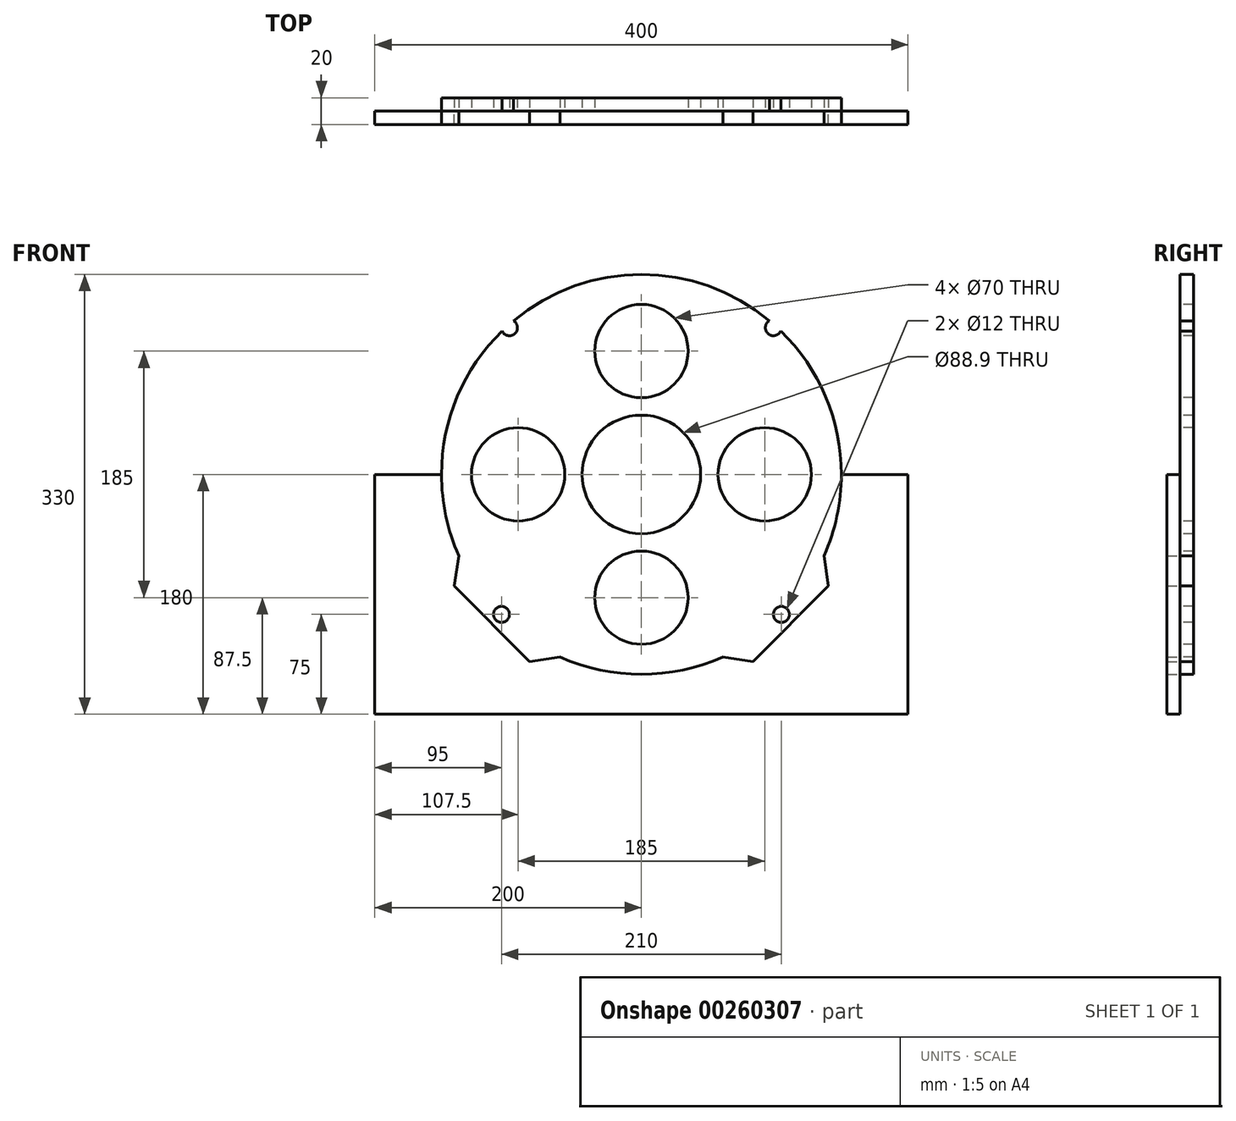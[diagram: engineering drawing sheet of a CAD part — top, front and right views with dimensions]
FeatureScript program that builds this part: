
annotation { "Feature Type Name" : "Feature", "Feature Type Description" : "" }
export const myFeature = defineFeature(function(context is Context, id is Id, definition is map)
    precondition{}
    {
        {
            var Q0;
            Q0=qCreatedBy(makeId("Front.planeOp"),FACE);
            var sketch = newSketch(context, id + "F0", { "sketchPlane" : qUnion([Q0])});
            skCircle(sketch, "E0", {"center": v(0, 0) * mm, "radius": 150 * mm});
            skCircle(sketch, "E1", {"center": v(0, 0) * mm, "radius": 140 * mm});
            skCircle(sketch, "E2", {"center": v(-99, 110) * mm, "radius": 6 * mm});
            skCircle(sketch, "E3.MirrorC", {"center": v(99, 110) * mm, "radius": 6 * mm});
            skCircle(sketch, "E4", {"center": v(105, -105) * mm, "radius": 6 * mm});
            skCircle(sketch, "E5.MirrorC", {"center": v(-105, -105) * mm, "radius": 6 * mm});
            skArc(sketch, "E6", {"start": v(-108.87, 103.18) * mm, "mid": v(-107.03, 118.92) * mm, "end": v(-91.18, 119.1) * mm});
            skArc(sketch, "E7", {"start": v(91.18, 119.1) * mm, "mid": v(107.03, 118.92) * mm, "end": v(108.87, 103.18) * mm});
            skLineSegment(sketch, "E8", {"start": v(-105, -105) * mm, "end": v(-112.07, -112.07) * mm});
            skLineSegment(sketch, "E9", {"start": v(-112.07, -112.07) * mm, "end": v(-83.79, -140.36) * mm});
            skLineSegment(sketch, "E10.MirrorCS", {"start": v(-112.07, -112.07) * mm, "end": v(-140.36, -83.79) * mm});
            skLineSegment(sketch, "E11", {"start": v(-140.36, -83.79) * mm, "end": v(-137.02, -61.03) * mm});
            skLineSegment(sketch, "E12.MirrorCS", {"start": v(-83.79, -140.36) * mm, "end": v(-61.03, -137.02) * mm});
            skLineSegment(sketch, "E13.MirrorCS", {"start": v(140.36, -83.79) * mm, "end": v(137.02, -61.03) * mm});
            skLineSegment(sketch, "E14.MirrorCS", {"start": v(112.07, -112.07) * mm, "end": v(140.36, -83.79) * mm});
            skLineSegment(sketch, "E15.MirrorCS", {"start": v(112.07, -112.07) * mm, "end": v(83.79, -140.36) * mm});
            skLineSegment(sketch, "E16.MirrorCS", {"start": v(83.79, -140.36) * mm, "end": v(61.03, -137.02) * mm});
            skCircle(sketch, "E17", {"center": v(0, 0) * mm, "radius": 44.45 * mm});
            skCircle(sketch, "E18", {"center": v(0, 92.5) * mm, "radius": 35 * mm});
            skCircle(sketch, "E19.MirrorC", {"center": v(0, -92.5) * mm, "radius": 35 * mm});
            skCircle(sketch, "E20", {"center": v(0, 0) * mm, "radius": 92.5 * mm});
            skCircle(sketch, "E21", {"center": v(92.5, 0) * mm, "radius": 35 * mm});
            skCircle(sketch, "E22", {"center": v(-92.5, 0) * mm, "radius": 35 * mm});
            skSolve(sketch);
        }
        {
            var Q0;
            Q0=makeQuery(id+"F0.imprint","IMPRINT",FACE,{"disambiguationData":[TD([[makeQuery(id+"F0.imprint","IMPRINT",EDGE,{"derivedFrom":sQuery(id+"F0.wireOp",EDGE,"E1")}),1.0]])]});
            var Q1;
            Q1=makeQuery(id+"F0.imprint","IMPRINT",FACE,{"disambiguationData":[TD([[makeQuery(id+"F0.imprint","IMPRINT",EDGE,{"derivedFrom":sQuery(id+"F0.wireOp",EDGE,"E17")}),-1.0]])]});
            var Q2;
            {var subQ0=sQuery(id+"F0.wireOp",EDGE,"E9");Q2=makeQuery(id+"F0.imprint","IMPRINT",FACE,{"disambiguationData":[TD([[makeQuery(id+"F0.imprint","IMPRINT",EDGE,{"derivedFrom":subQ0}),1.0]])]});}
            var Q3;
            Q3=makeQuery(id+"F0.imprint","IMPRINT",FACE,{"disambiguationData":[TD([[makeQuery(id+"F0.imprint","IMPRINT",EDGE,{"derivedFrom":sQuery(id+"F0.wireOp",EDGE,"E1")}),-1.0]])]});
            var Q4;
            {var subQ0=sQuery(id+"F0.wireOp",EDGE,"E10.MirrorCS");Q4=makeQuery(id+"F0.imprint","IMPRINT",FACE,{"disambiguationData":[TD([[makeQuery(id+"F0.imprint","IMPRINT",EDGE,{"derivedFrom":subQ0}),-1.0]])]});}
            var Q5;
            {var subQ0=sQuery(id+"F0.wireOp",EDGE,"E13.MirrorCS");Q5=makeQuery(id+"F0.imprint","IMPRINT",FACE,{"disambiguationData":[TD([[makeQuery(id+"F0.imprint","IMPRINT",EDGE,{"derivedFrom":subQ0}),1.0]])]});}
            var Q6;
            {var subQ0=sQuery(id+"F0.wireOp",EDGE,"E7");Q6=makeQuery(id+"F0.imprint","IMPRINT",FACE,{"disambiguationData":[TD([[makeQuery(id+"F0.imprint","IMPRINT",EDGE,{"derivedFrom":subQ0}),-1.0]])]});}
            var Q7;
            {var subQ0=sQuery(id+"F0.wireOp",EDGE,"E6");Q7=makeQuery(id+"F0.imprint","IMPRINT",FACE,{"disambiguationData":[TD([[makeQuery(id+"F0.imprint","IMPRINT",EDGE,{"derivedFrom":subQ0}),-1.0]])]});}
            extrude(context, id + "F1", {"entities" : qUnion([Q0, Q1, Q2, Q3, Q4, Q5, Q6, Q7]), "oppositeDirection" : true, "depth" : 10 * mm});
        }
        {
            var Q0;
            Q0=makeQuery(id+"F1.opExtrude","CAP_FACE",FACE,{"disambiguationData":[OSD([sQuery(id+"F0.wireOp",EDGE,"E0"),sQuery(id+"F0.wireOp",EDGE,"E2"),sQuery(id+"F0.wireOp",EDGE,"E3.MirrorC"),sQuery(id+"F0.wireOp",EDGE,"E4"),sQuery(id+"F0.wireOp",EDGE,"E5.MirrorC"),sQuery(id+"F0.wireOp",EDGE,"E6"),sQuery(id+"F0.wireOp",EDGE,"E7"),sQuery(id+"F0.wireOp",EDGE,"E9"),sQuery(id+"F0.wireOp",EDGE,"E10.MirrorCS"),sQuery(id+"F0.wireOp",EDGE,"E11"),sQuery(id+"F0.wireOp",EDGE,"E12.MirrorCS"),sQuery(id+"F0.wireOp",EDGE,"E13.MirrorCS"),sQuery(id+"F0.wireOp",EDGE,"E14.MirrorCS"),sQuery(id+"F0.wireOp",EDGE,"E15.MirrorCS"),sQuery(id+"F0.wireOp",EDGE,"E16.MirrorCS"),sQuery(id+"F0.wireOp",EDGE,"E17"),sQuery(id+"F0.wireOp",EDGE,"E18"),sQuery(id+"F0.wireOp",EDGE,"E19.MirrorC"),sQuery(id+"F0.wireOp",EDGE,"E21"),sQuery(id+"F0.wireOp",EDGE,"E22")])],"isStart":true});
            var sketch = newSketch(context, id + "F2", { "sketchPlane" : qUnion([Q0])});
            skCircle(sketch, "E23", {"center": v(0, 0) * mm, "radius": 135.99 * mm});
            skLineSegment(sketch, "E24", {"start": v(-135.99, 0) * mm, "end": v(-150, 0) * mm});
            skLineSegment(sketch, "E25", {"start": v(135.99, 0) * mm, "end": v(150, 0) * mm});
            skLineSegment(sketch, "E26", {"start": v(150, 0) * mm, "end": v(200, 0) * mm});
            skLineSegment(sketch, "E27", {"start": v(-150, 0) * mm, "end": v(-150, 0) * mm});
            skLineSegment(sketch, "E28", {"start": v(-200, 0) * mm, "end": v(-200, -180) * mm});
            skLineSegment(sketch, "E29", {"start": v(-200, -180) * mm, "end": v(200, -180) * mm});
            skLineSegment(sketch, "E30", {"start": v(200, -180) * mm, "end": v(200, 0) * mm});
            skLineSegment(sketch, "E31", {"start": v(-150, 0) * mm, "end": v(-200, 0) * mm});
            skSolve(sketch);
        }
        {
            var Q0;
            {var subQ5=sQuery(id+"F2.wireOp",EDGE,"E26");Q0=makeQuery(id+"F2.imprint","IMPRINT",FACE,{"disambiguationData":[TD([[makeQuery(id+"F2.imprint","IMPRINT",EDGE,{"derivedFrom":subQ5}),-1.0]])]});}
            extrude(context, id + "F3", {"entities" : qUnion([Q0]), "depth" : 10 * mm});
        }
    });
